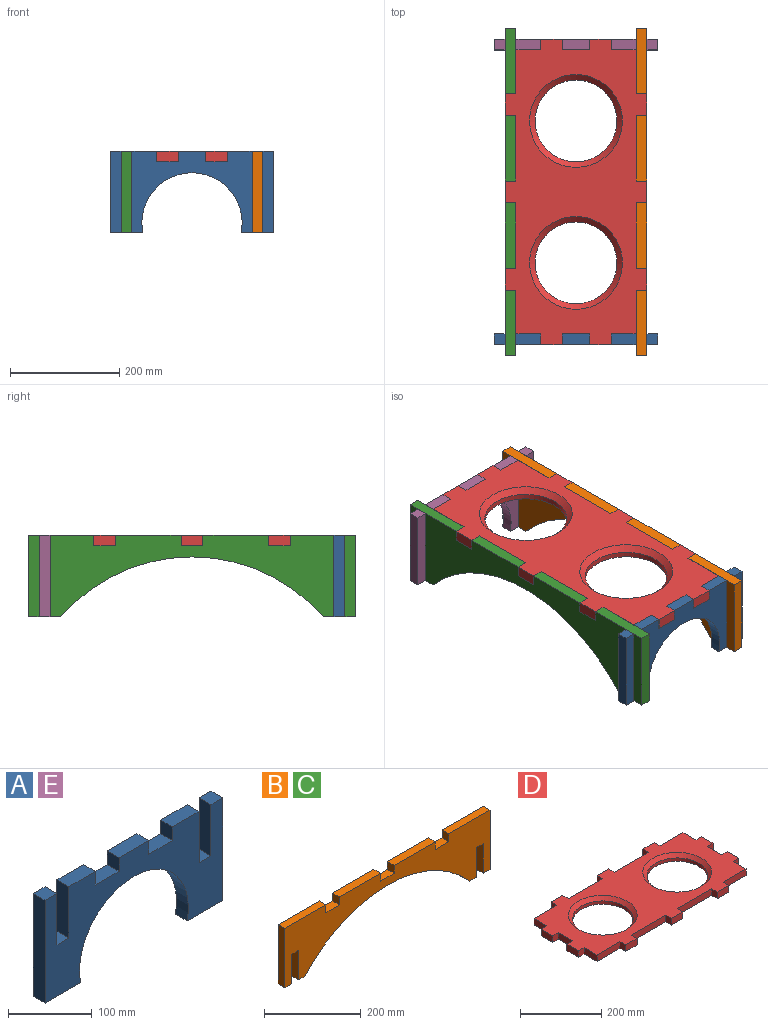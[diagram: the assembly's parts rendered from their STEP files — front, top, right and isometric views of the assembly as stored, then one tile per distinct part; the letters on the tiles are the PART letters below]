
ASSEMBLY  parts=5 mates=4
PART A: 24 faces, bbox 300x20x150 mm
  f0: plane 75x20mm, normal (1,0,0), area 1500mm2, adj f1,f21,f22,f23
  f1: plane 45x20mm, normal (0,0,1), area 900mm2, adj f0,f2,f22,f23
  f2: plane 20x20mm, normal (-1,0,0), area 400mm2, adj f1,f3,f22,f23
  f3: plane 40x20mm, normal (0,0,1), area 800mm2, adj f2,f4,f22,f23
  f4: plane 20x20mm, normal (1,0,0), area 400mm2, adj f3,f5,f22,f23
  f5: plane 50x20mm, normal (0,0,1), area 1000mm2, adj f4,f6,f22,f23
  f6: plane 20x20mm, normal (-1,0,0), area 400mm2, adj f5,f7,f22,f23
  f7: plane 40x20mm, normal (0,0,1), area 800mm2, adj f6,f8,f22,f23
  f8: plane 20x20mm, normal (1,0,0), area 400mm2, adj f7,f9,f22,f23
  f9: plane 45x20mm, normal (0,0,1), area 900mm2, adj f8,f10,f22,f23
  f10: plane 75x20mm, normal (-1,0,0), area 1500mm2, adj f9,f11,f22,f23
  f11: plane 20x20mm, normal (0,0,1), area 400mm2, adj f10,f12,f22,f23
  f12: plane 75x20mm, normal (1,0,0), area 1500mm2, adj f11,f13,f22,f23
  f13: plane 20x20mm, normal (0,0,1), area 400mm2, adj f12,f14,f22,f23
  f14: plane 150x20mm, normal (-1,0,0), area 3000mm2, adj f13,f15,f22,f23
  f15: plane 60x20mm, normal (0,0,-1), area 1200mm2, adj f14,f16,f22,f23
  f16: cylinder r=91.82mm len=183.64mm, axis (0,1,0), area 6501.2mm2, adj f15,f17,f22,f23
  f17: plane 60x20mm, normal (0,0,-1), area 1200mm2, adj f16,f18,f22,f23
  f18: plane 150x20mm, normal (1,0,0), area 3000mm2, adj f17,f19,f22,f23
  f19: plane 20x20mm, normal (0,0,1), area 400mm2, adj f18,f20,f22,f23
  f20: plane 75x20mm, normal (-1,0,0), area 1500mm2, adj f19,f21,f22,f23
  f21: plane 20x20mm, normal (0,0,1), area 400mm2, adj f0,f20,f22,f23
  f22: plane 300x150mm, normal (0,-1,0), area 23840.3mm2, adj f0,f1,f2,f3,f4,f5,f6,f7
  f23: plane 300x150mm, normal (0,1,0), area 23840.3mm2, adj f0,f1,f2,f3,f4,f5,f6,f7
PART B: 28 faces, bbox 600x20x150 mm
  f0: plane 20x20mm, normal (1,0,0), area 400mm2, adj f1,f25,f26,f27
  f1: plane 120x20mm, normal (0,0,1), area 2400mm2, adj f0,f2,f26,f27
  f2: plane 150x20mm, normal (-1,0,0), area 3000mm2, adj f1,f3,f26,f27
  f3: plane 20x20mm, normal (0,0,-1), area 400mm2, adj f2,f4,f26,f27
  f4: plane 75x20mm, normal (1,0,0), area 1500mm2, adj f3,f5,f26,f27
  f5: plane 20x20mm, normal (0,0,-1), area 400mm2, adj f4,f6,f26,f27
  f6: plane 75x20mm, normal (-1,0,0), area 1500mm2, adj f5,f7,f26,f27
  f7: plane 20x20mm, normal (0,0,-1), area 400mm2, adj f6,f8,f26,f27
  f8: cylinder r=316.82mm len=480mm, axis (0,1,0), area 10892.5mm2, adj f7,f9,f26,f27
  f9: plane 20x20mm, normal (0,0,-1), area 400mm2, adj f8,f10,f26,f27
  f10: plane 75x20mm, normal (1,0,0), area 1500mm2, adj f9,f11,f26,f27
  f11: plane 20x20mm, normal (0,0,-1), area 400mm2, adj f10,f12,f26,f27
  f12: plane 75x20mm, normal (-1,0,0), area 1500mm2, adj f11,f13,f26,f27
  f13: plane 20x20mm, normal (0,0,-1), area 400mm2, adj f12,f14,f26,f27
  f14: plane 150x20mm, normal (1,0,0), area 3000mm2, adj f13,f15,f26,f27
  f15: plane 120x20mm, normal (0,0,1), area 2400mm2, adj f14,f16,f26,f27
  f16: plane 20x20mm, normal (-1,0,0), area 400mm2, adj f15,f17,f26,f27
  f17: plane 40x20mm, normal (0,0,1), area 800mm2, adj f16,f18,f26,f27
  f18: plane 20x20mm, normal (1,0,0), area 400mm2, adj f17,f19,f26,f27
  f19: plane 120x20mm, normal (0,0,1), area 2400mm2, adj f18,f20,f26,f27
  f20: plane 20x20mm, normal (-1,0,0), area 400mm2, adj f19,f21,f26,f27
  f21: plane 40x20mm, normal (0,0,1), area 800mm2, adj f20,f22,f26,f27
  f22: plane 20x20mm, normal (1,0,0), area 400mm2, adj f21,f23,f26,f27
  f23: plane 120x20mm, normal (0,0,1), area 2400mm2, adj f22,f24,f26,f27
  f24: plane 20x20mm, normal (-1,0,0), area 400mm2, adj f23,f25,f26,f27
  f25: plane 40x20mm, normal (0,0,1), area 800mm2, adj f0,f24,f26,f27
  f26: plane 600x150mm, normal (0,-1,0), area 47962.7mm2, adj f0,f1,f2,f3,f4,f5,f6,f7
  f27: plane 600x150mm, normal (0,1,0), area 47962.7mm2, adj f0,f1,f2,f3,f4,f5,f6,f7
PART C: same geometry as B
PART D: 50 faces, bbox 560x260x20 mm
  f0: plane 20x20mm, normal (1,0,0), area 400mm2, adj f1,f44,f46,f47
  f1: plane 120x20mm, normal (0,-1,0), area 2400mm2, adj f0,f2,f46,f47
  f2: plane 20x20mm, normal (-1,0,0), area 400mm2, adj f1,f3,f46,f47
  f3: plane 40x20mm, normal (0,-1,0), area 800mm2, adj f2,f4,f46,f47
  f4: plane 20x20mm, normal (1,0,0), area 400mm2, adj f3,f5,f46,f47
  f5: plane 80x20mm, normal (0,-1,0), area 1600mm2, adj f4,f6,f46,f47
  f6: plane 45x20mm, normal (1,0,0), area 900mm2, adj f5,f7,f46,f47
  f7: plane 20x20mm, normal (0,-1,0), area 400mm2, adj f6,f8,f46,f47
  f8: plane 40x20mm, normal (1,0,0), area 800mm2, adj f7,f9,f46,f47
  f9: plane 20x20mm, normal (0,1,0), area 400mm2, adj f8,f10,f46,f47
  f10: plane 50x20mm, normal (1,0,0), area 1000mm2, adj f9,f11,f46,f47
  f11: plane 20x20mm, normal (0,-1,0), area 400mm2, adj f10,f12,f46,f47
  f12: plane 40x20mm, normal (1,0,0), area 800mm2, adj f11,f13,f46,f47
  f13: plane 20x20mm, normal (0,1,0), area 400mm2, adj f12,f14,f46,f47
  f14: plane 45x20mm, normal (1,0,0), area 900mm2, adj f13,f15,f46,f47
  f15: plane 80x20mm, normal (0,1,0), area 1600mm2, adj f14,f16,f46,f47
  f16: plane 20x20mm, normal (1,0,0), area 400mm2, adj f15,f17,f46,f47
  f17: plane 40x20mm, normal (0,1,0), area 800mm2, adj f16,f18,f46,f47
  f18: plane 20x20mm, normal (-1,0,0), area 400mm2, adj f17,f19,f46,f47
  f19: plane 120x20mm, normal (0,1,0), area 2400mm2, adj f18,f20,f46,f47
  f20: plane 20x20mm, normal (1,0,0), area 400mm2, adj f19,f21,f46,f47
  f21: plane 40x20mm, normal (0,1,0), area 800mm2, adj f20,f22,f46,f47
  f22: plane 20x20mm, normal (-1,0,0), area 400mm2, adj f21,f23,f46,f47
  f23: plane 120x20mm, normal (0,1,0), area 2400mm2, adj f22,f24,f46,f47
  f24: plane 20x20mm, normal (1,0,0), area 400mm2, adj f23,f25,f46,f47
  f25: plane 40x20mm, normal (0,1,0), area 800mm2, adj f24,f26,f46,f47
  f26: plane 20x20mm, normal (-1,0,0), area 400mm2, adj f25,f27,f46,f47
  f27: plane 80x20mm, normal (0,1,0), area 1600mm2, adj f26,f28,f46,f47
  f28: plane 45x20mm, normal (-1,0,0), area 900mm2, adj f27,f29,f46,f47
  f29: plane 20x20mm, normal (0,1,0), area 400mm2, adj f28,f30,f46,f47
  f30: plane 40x20mm, normal (-1,0,0), area 800mm2, adj f29,f31,f46,f47
  f31: plane 20x20mm, normal (0,-1,0), area 400mm2, adj f30,f32,f46,f47
  f32: plane 50x20mm, normal (-1,0,0), area 1000mm2, adj f31,f33,f46,f47
  f33: plane 20x20mm, normal (0,1,0), area 400mm2, adj f32,f34,f46,f47
  f34: plane 40x20mm, normal (-1,0,0), area 800mm2, adj f33,f35,f46,f47
  f35: plane 20x20mm, normal (0,-1,0), area 400mm2, adj f34,f36,f46,f47
  f36: plane 45x20mm, normal (-1,0,0), area 900mm2, adj f35,f37,f46,f47
  f37: plane 80x20mm, normal (0,-1,0), area 1600mm2, adj f36,f38,f46,f47
  f38: plane 20x20mm, normal (-1,0,0), area 400mm2, adj f37,f39,f46,f47
  f39: plane 40x20mm, normal (0,-1,0), area 800mm2, adj f38,f40,f46,f47
  f40: plane 20x20mm, normal (1,0,0), area 400mm2, adj f39,f41,f46,f47
  f41: plane 120x20mm, normal (0,-1,0), area 2400mm2, adj f40,f42,f46,f47
  f42: plane 20x20mm, normal (-1,0,0), area 400mm2, adj f41,f44,f46,f47
  f43: cylinder r=75mm len=150mm, axis (0,0,-1), area 4712.4mm2, adj f47,f48
  f44: plane 40x20mm, normal (0,-1,0), area 800mm2, adj f0,f42,f46,f47
  f45: cylinder r=75mm len=150mm, axis (0,0,-1), area 4712.4mm2, adj f47,f49
  f46: plane 560x260mm, normal (0,0,1), area 77004mm2, adj f0,f1,f2,f3,f4,f5,f6,f7
  f47: plane 560x260mm, normal (0,0,-1), area 87057.1mm2, adj f0,f1,f2,f3,f4,f5,f6,f7
  f48: cone r=75mm half-angle=45deg, axis (0,0,1), area 7108.6mm2, adj f43,f46
  f49: cone r=75mm half-angle=45deg, axis (0,0,1), area 7108.6mm2, adj f45,f46
PART E: same geometry as A
PLACE A t=(268.46,387.05,48.32)mm
PLACE B rot(axis=(0,0,-1),90deg) t=(548.46,947.05,48.32)mm
PLACE C rot(axis=(0,0,1),90deg) t=(288.46,347.05,48.32)mm
PLACE D rot(axis=(0,0,1),90deg) t=(528.46,387.05,178.32)mm
PLACE E t=(268.46,927.05,48.32)mm
MATE fastened C.f5 <-> A.f11  axis (0,0,-1) through (298.46,377.05,123.32)mm
MATE fastened B.f5 <-> E.f21  axis (0,0,-1) through (538.46,917.05,123.32)mm
MATE fastened C.f11 <-> E.f11  axis (0,0,-1) through (298.46,917.05,123.32)mm
MATE fastened D.f35 <-> A.f2  axis (1,0,0) through (483.46,377.05,188.32)mm
